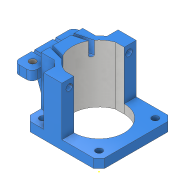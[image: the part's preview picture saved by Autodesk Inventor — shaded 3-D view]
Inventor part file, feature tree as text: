
AUTODESK INVENTOR PART (.ipt)
format: ipt  version: 2020 (Build 240168000, 168)  size: 411,136 bytes
history: native  units: in
note: dims shown in document units (in); Inventor stores cm internally (conversion verified against a paired STEP export)
features: sketch x23, extrude x19, mirror x9, thicken_offset x4, chamfer x2, pattern_linear x1, plane x1, sweep x1, fillet x1
ambient origin geometry x8: Origin, YZ Plane, XZ Plane, XY Plane, X Axis, Y Axis, Z Axis, Center Point
bodies: Solid1 (feature_tree)
feature tree (61):
  extrude  "Extrusion1"  Depth=1.6142in
  extrude  "Extrusion2"  Depth=0.1969in
  extrude  "Extrusion3"  Depth=0.1969in
  pattern_linear  "Rectangular Pattern1"  Count1=2 Spacing1=1.2205in
  extrude  "Extrusion4"  Depth=0.9567in
  extrude  "Extrusion5"  Depth=1.2598in TaperAngle=0.0deg
  extrude  "Extrusion6"  Depth=0.3937in
  plane  "Work Plane1"
  mirror  "Mirror1"
  extrude  "Extrusion7"  [1 undecoded]
  extrude  "Extrusion8"  Depth=1.2598in TaperAngle=0.0deg
  mirror  "Mirror2"
  sketch  "Sketch10"  dims[d28=0.9055in d29=1.2598in d30=0.0in]
  sketch  "Sketch11"  dims[d31=165.0deg d32=0.063in]
  sweep  "Sweep1"
  mirror  "Mirror3"
  extrude  "Extrusion9"  TaperAngle=165.0deg  [1 undecoded]
  extrude  "Extrusion10"  TaperAngle=0.0deg  [1 undecoded]
  extrude  "Extrusion11"  Depth=0.1969in
  mirror  "Mirror4"
  extrude  "Extrusion12"  Depth=0.3937in TaperAngle=0.0deg
  mirror  "Mirror5"
  extrude  "Extrusion14"  Depth=0.1969in TaperAngle=0.0deg
  mirror  "Mirror6"
  extrude  "Extrusion15"  Depth=0.3937in
  chamfer  "Chamfer1"  Distance=0.9843in
  fillet  "Fillet1"  Radius=0.1181in
  extrude  "Extrusion16"  Depth=0.9843in TaperAngle=0.0deg
  mirror  "Mirror7"
  extrude  "Extrusion17"  Depth=0.1181in
  mirror  "Mirror8"
  chamfer  "Chamfer2"  Distance=0.1969in
  thicken_offset  "Thicken1"
  thicken_offset  "Thicken2"
  thicken_offset  "Thicken3"
  extrude  "Extrusion18"  Depth=0.1969in
  sketch  "Sketch23"  dims[d68=0.0984in d69=0.0in d70=0.1181in d71=0.0787in d72=0.481in]
  extrude  "Extrusion19"  Depth=0.1969in
  extrude  "Extrusion20"  Depth=0.1969in
  mirror  "Mirror9"
  thicken_offset  "Thicken4"
  sketch  "Sketch1"  dims[d0=1.6142in d1=1.6142in]
  sketch  "Sketch2"  dims[d2=0.1969in d3=0.0in d4=0.5906in]
  sketch  "Sketch3"  dims[d5=0.1969in d6=0.0in d7=0.1417in]
  sketch  "Sketch4"  dims[d8=0.1969in d9=0.0in d10=0.7874in d12=1.2205in]
  sketch  "Sketch5"  dims[d13=0.7874in d15=1.2205in d16=0.9567in]
  sketch  "Sketch6"  dims[d17=1.378in d18=1.2598in d19=0.0in]
  sketch  "Sketch8"  dims[d20=1.2598in d21=0.0in d22=0.3937in]
  sketch  "Sketch9"  dims[d23=1.2598in d24=0.0in d25=-0.8071in]
  sketch  "3D Sketch1"
  sketch  "Sketch12"  dims[d33=0.0394in d34=165.0deg]
  sketch  "Sketch13"  dims[d35=0.2756in d36=0.0in d37=0.0in d38=0.0in]
  sketch  "Sketch14"  dims[d39=0.9055in d40=0.1969in]
  sketch  "Sketch15"  dims[d41=0.3937in d42=0.0in d43=0.3937in d44=0.0in]
  sketch  "Sketch18"  dims[d45=0.1969in d46=0.0in d48=0.1969in d49=0.0in]
  sketch  "Sketch19"  dims[d54=0.0984in d55=0.0in d56=0.3937in]
  sketch  "Sketch20"  dims[d57=0.4724in d58=0.9843in d59=0.0in]
  sketch  "Sketch21"  dims[d60=0.3543in d61=0.0787in d62=0.481in d63=0.1181in]
  sketch  "Sketch22"  dims[d64=0.1417in d65=0.9843in d66=0.0in]
  sketch  "Sketch24"  dims[d73=0.1969in]
  sketch  "Sketch25"  dims[d74=0.1969in d75=0.1969in d76=0.1969in d77=0.1969in d78=0.1969in d79=0.1969in d80=0.0in d81=0.1417in d84=1.158in d85=1.5748in d86=0.0in d87=0.2756in d88=0.0315in d89=1.5748in d90=0.0in d91=0.0315in d92=0.0315in d93=0.0984in d94=0.0in]
note: 3 required parameter values undecoded (feature->parameter linkage not recoverable at this tier; creation-order binding heuristic only, values carry confidence <= 0.55)
